# Revit family: 51_D90-XGB- 25L
name_source: partatom
category: Equipos especializados
units: mm (PartAtom-declared; Revit-internal decimal feet)

## family parameters
Compartido = No
Corte con vacíos al cargar = No
Cota de conector redondo = Diámetro de uso
Punto de cálculo de habitación = No
Se basa en plano de trabajo = No
Siempre vertical = Sí
Tipo de pieza = Normal

## types (1)
- D90-XGB- 25L
    Alto = 39 cm
    Ancho = 59.5 cm
    Aprobaciones = CE/GS/CB/SAA
    Creado por = Unibim
    Descongelamiento = si
    Display = Digital
    Display Electrónico con paro = si
    Elevación por defecto = 0 cm
    Fabricante = Vatti
    Facilidad de uso = Microondas- Grill- Convección
    Fondo = 39.1 cm
    Instalación = Empotrado
    Interior = Easy Clean
    Luz interior = si
    Marco de Encastre = si
    Modelo = D90-XGB- 25L
    Modo de control = Control Digital
    Paneles = Vidrio -Acero Inox
    Peso = 18
    Plato Incorporado = si
    Potencia Grill = 1000W
    Potencia Microondas = 1400W
    Potencia Salida Microondas = 900W
    Programador de paro = si
    Puerta Vidiro = Panel Vidrio
    Selector de potencia = si
    Sistema de seguridad doble cierre = si
    Tamaño del producto = 390 x 595 x 391
    Temporizador = si
    Termostato con luz indicadora = si
    URL = www.vatti.cl
    Voltage/ Frecuencia = 220V/ 50Hz
    Volumen interior = 25 Litros
    _Plastico negro = _Plastico Negro

## geometry (parser evidence)
native form markers: Sweep x2
no freeform markers — native parametric forms only
